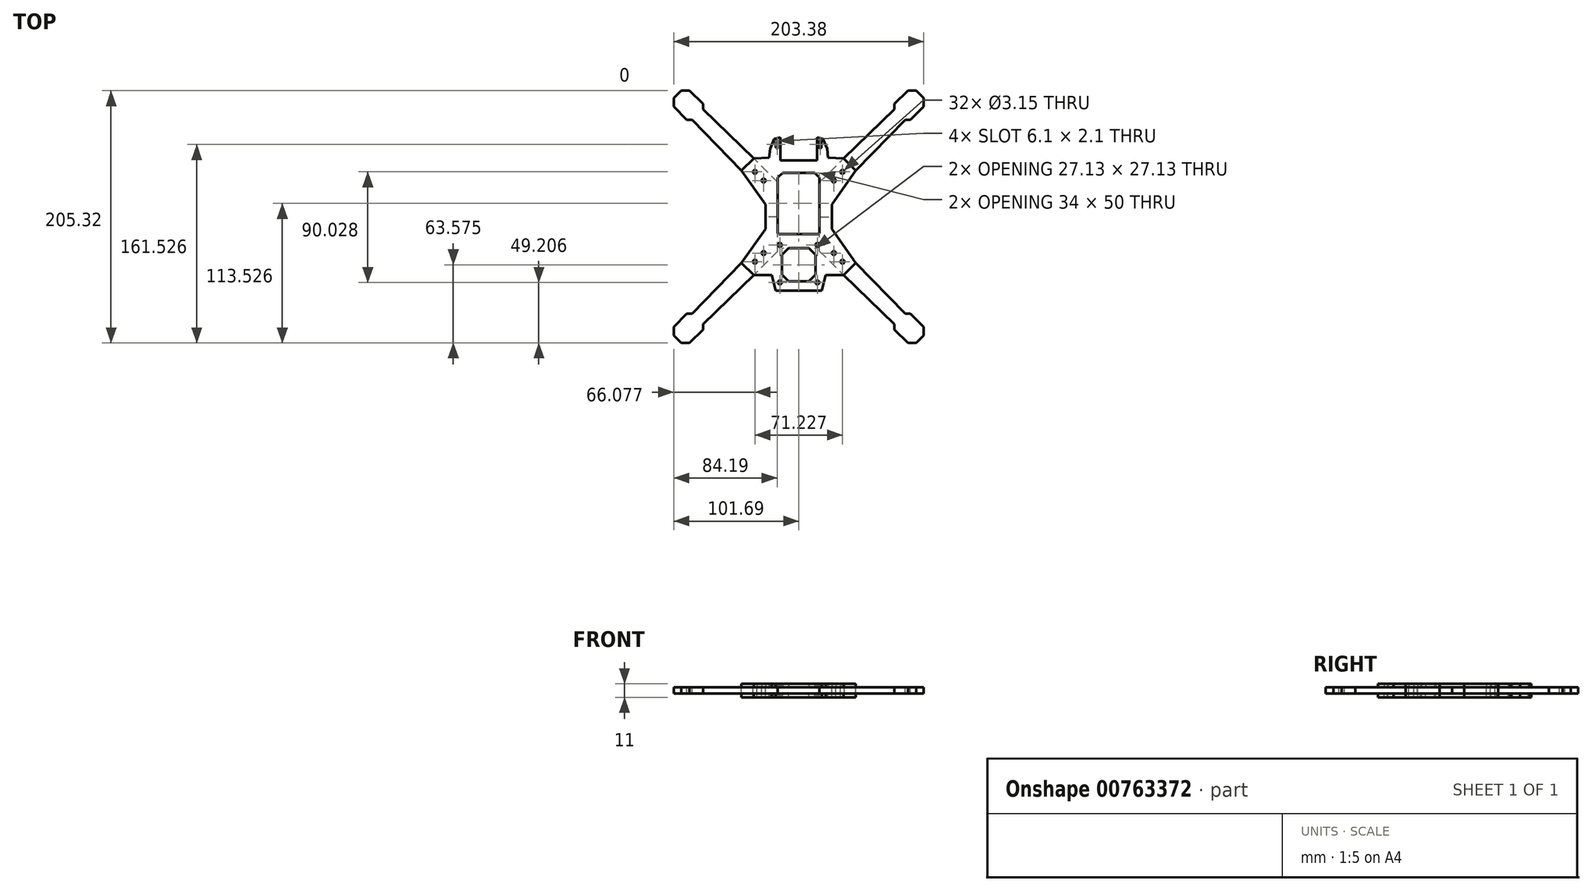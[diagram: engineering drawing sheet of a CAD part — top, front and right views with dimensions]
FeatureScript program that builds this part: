
annotation { "Feature Type Name" : "Feature", "Feature Type Description" : "" }
export const myFeature = defineFeature(function(context is Context, id is Id, definition is map)
    precondition{}
    {
        {
            assignVariable(context, id + "F0", {"name" : "SandwichThickness", "anyValue" : 3 * mm});
        }
        {
            assignVariable(context, id + "F1", {"name" : "ArmThickness", "anyValue" : 5 * mm});
        }
        {
            var Q0;
            Q0=qCreatedBy(makeId("Top.planeOp"),FACE);
            var sketch = newSketch(context, id + "F2", { "sketchPlane" : qUnion([Q0])});
            skCircle(sketch, "E0", {"center": v(-15.25, -22.95) * mm, "radius": 1.57 * mm});
            skCircle(sketch, "E1.MirrorC", {"center": v(15.25, -22.95) * mm, "radius": 1.57 * mm});
            skCircle(sketch, "E2", {"center": v(-15.25, -53.45) * mm, "radius": 1.57 * mm});
            skCircle(sketch, "E3.MirrorC", {"center": v(15.25, -53.45) * mm, "radius": 1.57 * mm});
            skLineSegment(sketch, "E4", {"start": v(-19.86, 63.27) * mm, "end": v(-23.2, 55.32) * mm});
            skLineSegment(sketch, "E5", {"start": v(-19.86, 63.27) * mm, "end": v(-15, 64.52) * mm});
            skLineSegment(sketch, "E6", {"start": v(-15, 64.52) * mm, "end": v(-15, 45.87) * mm});
            skLineSegment(sketch, "E7", {"start": v(-17, 31.8) * mm, "end": v(-17, -13.31) * mm});
            skLineSegment(sketch, "E8", {"start": v(-17, -13.31) * mm, "end": v(-16.18, -14.13) * mm});
            skLineSegment(sketch, "E9", {"start": v(-16.18, -14.13) * mm, "end": v(0, -14.13) * mm});
            skLineSegment(sketch, "E10.MirrorCS", {"start": v(14.55, -15.76) * mm, "end": v(0, -15.76) * mm});
            skArc(sketch, "E11.0.startCap", {"start": v(-18.55, 60.87) * mm, "mid": v(-17.5, 61.92) * mm, "end": v(-16.45, 60.87) * mm});
            skArc(sketch, "E11.0.endCap", {"start": v(-16.45, 56.87) * mm, "mid": v(-17.5, 55.82) * mm, "end": v(-18.55, 56.87) * mm});
            skLineSegment(sketch, "E11.0.left", {"start": v(-16.45, 60.87) * mm, "end": v(-16.45, 56.87) * mm});
            skLineSegment(sketch, "E11.0.right", {"start": v(-18.55, 60.87) * mm, "end": v(-18.55, 56.87) * mm});
            skLineSegment(sketch, "E12", {"start": v(0, 35.87) * mm, "end": v(-12.93, 35.87) * mm});
            skLineSegment(sketch, "E13", {"start": v(-12.93, 35.87) * mm, "end": v(-17, 31.8) * mm});
            skLineSegment(sketch, "E14", {"start": v(-36.6, 47.46) * mm, "end": v(-46.5, 37.56) * mm});
            skLineSegment(sketch, "E15", {"start": v(-46.5, 37.56) * mm, "end": v(-27, 10) * mm});
            skLineSegment(sketch, "E16", {"start": v(-27, 10) * mm, "end": v(-27, -10) * mm});
            skLineSegment(sketch, "E17", {"start": v(-27, -10) * mm, "end": v(-46.5, -37.56) * mm});
            skLineSegment(sketch, "E18", {"start": v(-46.5, -37.56) * mm, "end": v(-36.6, -47.46) * mm});
            skLineSegment(sketch, "E19", {"start": v(-36.6, -47.46) * mm, "end": v(-21.87, -47.46) * mm});
            skLineSegment(sketch, "E20", {"start": v(-21.87, -47.46) * mm, "end": v(-18.77, -60.18) * mm});
            skLineSegment(sketch, "E21", {"start": v(-18.77, -60.18) * mm, "end": v(0, -60.18) * mm});
            skLineSegment(sketch, "E22", {"start": v(-36.6, 47.46) * mm, "end": v(-23.99, 48.25) * mm});
            skLineSegment(sketch, "E23", {"start": v(-23.99, 48.25) * mm, "end": v(-23.2, 55.32) * mm});
            skCircle(sketch, "E24", {"center": v(-35.61, 36.57) * mm, "radius": 1.57 * mm});
            skLineSegment(sketch, "E25", {"start": v(-41.55, 42.51) * mm, "end": v(-28.54, 29.5) * mm, "construction": true});
            skCircle(sketch, "E26", {"center": v(-28.54, 29.5) * mm, "radius": 1.57 * mm});
            skLineSegment(sketch, "E27", {"start": v(-41.55, -42.51) * mm, "end": v(-28.54, -29.5) * mm, "construction": true});
            skLineSegment(sketch, "E28", {"start": v(-28.54, 29.5) * mm, "end": v(-28.54, -29.5) * mm, "construction": true});
            skLineSegment(sketch, "E29", {"start": v(-68.87, 0) * mm, "end": v(73.63, 0) * mm, "construction": true});
            skPoint(sketch, "E29.startSnap0", {"position": v(-28.54, 0) * mm});
            skCircle(sketch, "E30.MirrorC", {"center": v(-28.54, -29.5) * mm, "radius": 1.57 * mm});
            skCircle(sketch, "E31.MirrorC", {"center": v(-35.61, -36.57) * mm, "radius": 1.57 * mm});
            skLineSegment(sketch, "E32", {"start": v(18.01, -39.09) * mm, "end": v(-13.57, -39.09) * mm, "construction": true});
            skLineSegment(sketch, "E33", {"start": v(-13.57, -39.09) * mm, "end": v(-13.57, -47.25) * mm});
            skLineSegment(sketch, "E34", {"start": v(-13.57, -47.25) * mm, "end": v(-8.16, -52.65) * mm});
            skLineSegment(sketch, "E35", {"start": v(-8.16, -52.65) * mm, "end": v(0, -52.65) * mm});
            skLineSegment(sketch, "E36.MirrorCS", {"start": v(13.57, -39.09) * mm, "end": v(13.57, -47.25) * mm});
            skLineSegment(sketch, "E37.MirrorCS", {"start": v(13.57, -47.25) * mm, "end": v(8.16, -52.65) * mm});
            skLineSegment(sketch, "E38.MirrorCS", {"start": v(8.16, -52.65) * mm, "end": v(0, -52.65) * mm});
            skLineSegment(sketch, "E39.MirrorCS", {"start": v(-13.57, -39.09) * mm, "end": v(-13.57, -30.92) * mm});
            skLineSegment(sketch, "E40.MirrorCS", {"start": v(-13.57, -30.92) * mm, "end": v(-8.16, -25.52) * mm});
            skLineSegment(sketch, "E41.MirrorCS", {"start": v(-8.16, -25.52) * mm, "end": v(0, -25.52) * mm});
            skLineSegment(sketch, "E42.MirrorCS", {"start": v(8.16, -25.52) * mm, "end": v(0, -25.52) * mm});
            skLineSegment(sketch, "E43.MirrorCS", {"start": v(13.57, -30.92) * mm, "end": v(8.16, -25.52) * mm});
            skLineSegment(sketch, "E44.MirrorCS", {"start": v(13.57, -39.09) * mm, "end": v(13.57, -30.92) * mm});
            skLineSegment(sketch, "E45.MirrorCS", {"start": v(15, 64.52) * mm, "end": v(15, 45.87) * mm});
            skLineSegment(sketch, "E46.MirrorCS", {"start": v(19.86, 63.27) * mm, "end": v(15, 64.52) * mm});
            skLineSegment(sketch, "E47.MirrorCS", {"start": v(19.86, 63.27) * mm, "end": v(23.2, 55.32) * mm});
            skArc(sketch, "E48.MirrorCS", {"start": v(18.55, 60.87) * mm, "mid": v(17.5, 61.92) * mm, "end": v(16.45, 60.87) * mm});
            skLineSegment(sketch, "E49.MirrorCS", {"start": v(17.5, 60.87) * mm, "end": v(17.5, 56.87) * mm, "construction": true});
            skLineSegment(sketch, "E50.MirrorCS", {"start": v(18.55, 60.87) * mm, "end": v(18.55, 56.87) * mm});
            skLineSegment(sketch, "E51.MirrorCS", {"start": v(16.45, 60.87) * mm, "end": v(16.45, 56.87) * mm});
            skArc(sketch, "E52.MirrorCS", {"start": v(16.45, 56.87) * mm, "mid": v(17.5, 55.82) * mm, "end": v(18.55, 56.87) * mm});
            skLineSegment(sketch, "E53.MirrorCS", {"start": v(23.99, 48.25) * mm, "end": v(23.2, 55.32) * mm});
            skLineSegment(sketch, "E54.MirrorCS", {"start": v(36.6, 47.46) * mm, "end": v(23.99, 48.25) * mm});
            skLineSegment(sketch, "E55.MirrorCS", {"start": v(36.6, 47.46) * mm, "end": v(46.5, 37.56) * mm});
            skLineSegment(sketch, "E56.MirrorCS", {"start": v(46.5, 37.56) * mm, "end": v(27, 10) * mm});
            skCircle(sketch, "E57.MirrorC", {"center": v(35.61, 36.57) * mm, "radius": 1.57 * mm});
            skCircle(sketch, "E58.MirrorC", {"center": v(28.54, 29.5) * mm, "radius": 1.57 * mm});
            skCircle(sketch, "E59.MirrorC", {"center": v(28.54, -29.5) * mm, "radius": 1.57 * mm});
            skCircle(sketch, "E60.MirrorC", {"center": v(35.61, -36.57) * mm, "radius": 1.57 * mm});
            skLineSegment(sketch, "E61.MirrorCS", {"start": v(27, -10) * mm, "end": v(46.5, -37.56) * mm});
            skLineSegment(sketch, "E62.MirrorCS", {"start": v(27, 10) * mm, "end": v(27, -10) * mm});
            skLineSegment(sketch, "E63.MirrorCS", {"start": v(46.5, -37.56) * mm, "end": v(36.6, -47.46) * mm});
            skLineSegment(sketch, "E64.MirrorCS", {"start": v(36.6, -47.46) * mm, "end": v(21.87, -47.46) * mm});
            skLineSegment(sketch, "E65.MirrorCS", {"start": v(21.87, -47.46) * mm, "end": v(18.77, -60.18) * mm});
            skLineSegment(sketch, "E66.MirrorCS", {"start": v(18.77, -60.18) * mm, "end": v(0, -60.18) * mm});
            skPoint(sketch, "E67", {"position": v(-17.5, 58.87) * mm});
            skLineSegment(sketch, "E68.MirrorCS", {"start": v(0, 35.87) * mm, "end": v(12.93, 35.87) * mm});
            skLineSegment(sketch, "E69.MirrorCS", {"start": v(12.93, 35.87) * mm, "end": v(17, 31.8) * mm});
            skLineSegment(sketch, "E70.MirrorCS", {"start": v(17, 31.8) * mm, "end": v(17, -13.31) * mm});
            skLineSegment(sketch, "E71.MirrorCS", {"start": v(16.18, -14.13) * mm, "end": v(0, -14.13) * mm});
            skLineSegment(sketch, "E72.MirrorCS", {"start": v(17, -13.31) * mm, "end": v(16.18, -14.13) * mm});
            skLineSegment(sketch, "E73", {"start": v(-17.5, 60.87) * mm, "end": v(-17.5, 56.87) * mm, "construction": true});
            skLineSegment(sketch, "E74", {"start": v(-15, 45.87) * mm, "end": v(0, 45.87) * mm});
            skLineSegment(sketch, "E75.MirrorCS", {"start": v(15, 45.87) * mm, "end": v(0, 45.87) * mm});
            skSolve(sketch);
        }
        {
            var Q0;
            Q0=makeQuery(id+"F2.imprint","IMPRINT",FACE,{"disambiguationData":[TD([[makeQuery(id+"F2.imprint","IMPRINT",EDGE,{"derivedFrom":sQuery(id+"F2.wireOp",EDGE,"E0")}),-1.0]])]});
            var sketch = newSketch(context, id + "F3", { "sketchPlane" : qUnion([Q0])});
            skCircle(sketch, "E76.0", {"center": v(-35.61, 36.57) * mm, "radius": 1.57 * mm});
            skCircle(sketch, "E77.0", {"center": v(-28.54, 29.5) * mm, "radius": 1.57 * mm});
            skLineSegment(sketch, "E78.0", {"start": v(-46.5, 37.56) * mm, "end": v(-27, 10) * mm});
            skPoint(sketch, "E79.0", {"position": v(-36.6, 47.46) * mm});
            skLineSegment(sketch, "E80", {"start": v(-17, 28.03) * mm, "end": v(-36.6, 47.46) * mm});
            skLineSegment(sketch, "E81", {"start": v(-36.6, 47.46) * mm, "end": v(-77.83, 87.54) * mm});
            skLineSegment(sketch, "E82.MirrorCS", {"start": v(-46.5, 37.56) * mm, "end": v(-86.58, 78.8) * mm});
            skLineSegment(sketch, "E83", {"start": v(-77.83, 87.54) * mm, "end": v(-77.83, 91.94) * mm});
            skLineSegment(sketch, "E84", {"start": v(-77.83, 91.94) * mm, "end": v(-88.86, 102.66) * mm});
            skLineSegment(sketch, "E85", {"start": v(-88.86, 102.66) * mm, "end": v(-95.6, 102.66) * mm});
            skLineSegment(sketch, "E86.MirrorCS", {"start": v(-86.58, 78.8) * mm, "end": v(-90.98, 78.8) * mm});
            skLineSegment(sketch, "E87.MirrorCS", {"start": v(-90.98, 78.8) * mm, "end": v(-101.7, 89.82) * mm});
            skLineSegment(sketch, "E88.MirrorCS", {"start": v(-101.7, 89.82) * mm, "end": v(-101.7, 96.57) * mm});
            skLineSegment(sketch, "E89", {"start": v(-95.6, 102.66) * mm, "end": v(-101.7, 96.57) * mm});
            skLineSegment(sketch, "E90", {"start": v(-27, 10) * mm, "end": v(-27, 0) * mm});
            skLineSegment(sketch, "E91", {"start": v(-17, 0) * mm, "end": v(-27, 0) * mm});
            skLineSegment(sketch, "E92", {"start": v(-17, 28.03) * mm, "end": v(-17, 0) * mm});
            skSolve(sketch);
        }
        {
            var Q0;
            Q0 = qSketchRegion(id + "F2", true);
            extrude(context, id + "F4", {"entities" : qUnion([Q0]), "depth" : getVariable(context, 'SandwichThickness'), "offsetDistance" : 25 * mm});
        }
        {
            var Q0;
            Q0 = qSketchRegion(id + "F3", true);
            extrude(context, id + "F5", {"entities" : qUnion([Q0]), "oppositeDirection" : true, "depth" : getVariable(context, 'ArmThickness'), "offsetDistance" : 25 * mm});
        }
        {
            var Q0;
            Q0=makeQuery(id+"F5.opExtrude","SWEPT_BODY",BODY,{"disambiguationData":[OSD([sQuery(id+"F3.wireOp",EDGE,"E76.0"),sQuery(id+"F3.wireOp",EDGE,"E77.0"),sQuery(id+"F3.wireOp",EDGE,"E78.0"),sQuery(id+"F3.wireOp",EDGE,"ryfLNu9Q-lvBm-nTtp-5XZK-GBmvkfGpwlt8"),sQuery(id+"F3.wireOp",EDGE,"jJSJpg1Z-H1VB-TZbG-EUJu-PynuGd8tt2l3"),sQuery(id+"F3.wireOp",EDGE,"NvUQPJ1X-drPx-f47S-Xc06-5eFbwI9bCRaz"),sQuery(id+"F3.wireOp",EDGE,"E80"),sQuery(id+"F3.wireOp",EDGE,"E81"),sQuery(id+"F3.wireOp",EDGE,"E82.MirrorCS"),sQuery(id+"F3.wireOp",EDGE,"E83"),sQuery(id+"F3.wireOp",EDGE,"E84"),sQuery(id+"F3.wireOp",EDGE,"E85"),sQuery(id+"F3.wireOp",EDGE,"E86.MirrorCS"),sQuery(id+"F3.wireOp",EDGE,"E87.MirrorCS"),sQuery(id+"F3.wireOp",EDGE,"E88.MirrorCS"),sQuery(id+"F3.wireOp",EDGE,"E89")])]});
            var Q1;
            Q1=qCreatedBy(makeId("Right.planeOp"),FACE);
            mirror(context, id + "F6", {"entities" : qUnion([Q0]), "mirrorPlane" : qUnion([Q1])});
        }
        {
            var Q0;
            Q0=makeQuery(id+"F5.opExtrude","SWEPT_BODY",BODY,{"disambiguationData":[OSD([sQuery(id+"F3.wireOp",EDGE,"E76.0"),sQuery(id+"F3.wireOp",EDGE,"E77.0"),sQuery(id+"F3.wireOp",EDGE,"E78.0"),sQuery(id+"F3.wireOp",EDGE,"ryfLNu9Q-lvBm-nTtp-5XZK-GBmvkfGpwlt8"),sQuery(id+"F3.wireOp",EDGE,"jJSJpg1Z-H1VB-TZbG-EUJu-PynuGd8tt2l3"),sQuery(id+"F3.wireOp",EDGE,"NvUQPJ1X-drPx-f47S-Xc06-5eFbwI9bCRaz"),sQuery(id+"F3.wireOp",EDGE,"E80"),sQuery(id+"F3.wireOp",EDGE,"E81"),sQuery(id+"F3.wireOp",EDGE,"E82.MirrorCS"),sQuery(id+"F3.wireOp",EDGE,"E83"),sQuery(id+"F3.wireOp",EDGE,"E84"),sQuery(id+"F3.wireOp",EDGE,"E85"),sQuery(id+"F3.wireOp",EDGE,"E86.MirrorCS"),sQuery(id+"F3.wireOp",EDGE,"E87.MirrorCS"),sQuery(id+"F3.wireOp",EDGE,"E88.MirrorCS"),sQuery(id+"F3.wireOp",EDGE,"E89")])]});
            var Q1;
            Q1=makeQuery(id+"F6.opPattern","COPY",BODY,{"derivedFrom":makeQuery(id+"F5.opExtrude","SWEPT_BODY",BODY,{"disambiguationData":[OSD([sQuery(id+"F3.wireOp",EDGE,"E76.0"),sQuery(id+"F3.wireOp",EDGE,"E77.0"),sQuery(id+"F3.wireOp",EDGE,"E78.0"),sQuery(id+"F3.wireOp",EDGE,"ryfLNu9Q-lvBm-nTtp-5XZK-GBmvkfGpwlt8"),sQuery(id+"F3.wireOp",EDGE,"jJSJpg1Z-H1VB-TZbG-EUJu-PynuGd8tt2l3"),sQuery(id+"F3.wireOp",EDGE,"NvUQPJ1X-drPx-f47S-Xc06-5eFbwI9bCRaz"),sQuery(id+"F3.wireOp",EDGE,"E80"),sQuery(id+"F3.wireOp",EDGE,"E81"),sQuery(id+"F3.wireOp",EDGE,"E82.MirrorCS"),sQuery(id+"F3.wireOp",EDGE,"E83"),sQuery(id+"F3.wireOp",EDGE,"E84"),sQuery(id+"F3.wireOp",EDGE,"E85"),sQuery(id+"F3.wireOp",EDGE,"E86.MirrorCS"),sQuery(id+"F3.wireOp",EDGE,"E87.MirrorCS"),sQuery(id+"F3.wireOp",EDGE,"E88.MirrorCS"),sQuery(id+"F3.wireOp",EDGE,"E89")])]}),"instanceName":"1"});
            var Q2;
            Q2=qCreatedBy(makeId("Front.planeOp"),FACE);
            mirror(context, id + "F7", {"entities" : qUnion([Q0, Q1]), "mirrorPlane" : qUnion([Q2])});
        }
        {
            var Q0;
            Q0=makeQuery(id+"F4.opExtrude","CAP_FACE",FACE,{"disambiguationData":[OSD([sQuery(id+"F2.wireOp",EDGE,"E0"),sQuery(id+"F2.wireOp",EDGE,"E1.MirrorC"),sQuery(id+"F2.wireOp",EDGE,"E2"),sQuery(id+"F2.wireOp",EDGE,"E3.MirrorC"),sQuery(id+"F2.wireOp",EDGE,"E4"),sQuery(id+"F2.wireOp",EDGE,"E5"),sQuery(id+"F2.wireOp",EDGE,"E6"),sQuery(id+"F2.wireOp",EDGE,"E7"),sQuery(id+"F2.wireOp",EDGE,"E8"),sQuery(id+"F2.wireOp",EDGE,"E9"),sQuery(id+"F2.wireOp",EDGE,"e5299873-a759-4b57-8e80-d9d10e7549ee3.MirrorCS"),sQuery(id+"F2.wireOp",EDGE,"E10.MirrorCS"),sQuery(id+"F2.wireOp",EDGE,"e5299873-a759-4b57-8e80-d9d10e7549ee9.MirrorCS"),sQuery(id+"F2.wireOp",EDGE,"E11.0.startCap"),sQuery(id+"F2.wireOp",EDGE,"E11.0.endCap"),sQuery(id+"F2.wireOp",EDGE,"E11.0.left"),sQuery(id+"F2.wireOp",EDGE,"E11.0.right"),sQuery(id+"F2.wireOp",EDGE,"E12"),sQuery(id+"F2.wireOp",EDGE,"E13"),sQuery(id+"F2.wireOp",EDGE,"9a270ce7-c52f-46a5-af98-66fd616d05850.MirrorCS"),sQuery(id+"F2.wireOp",EDGE,"67116adb-6c2d-4a79-b561-e3b161ec186f0.MirrorCS"),sQuery(id+"F2.wireOp",EDGE,"E14"),sQuery(id+"F2.wireOp",EDGE,"E15"),sQuery(id+"F2.wireOp",EDGE,"E16"),sQuery(id+"F2.wireOp",EDGE,"E17"),sQuery(id+"F2.wireOp",EDGE,"E18"),sQuery(id+"F2.wireOp",EDGE,"E19"),sQuery(id+"F2.wireOp",EDGE,"E20"),sQuery(id+"F2.wireOp",EDGE,"E21"),sQuery(id+"F2.wireOp",EDGE,"1nEM5pcN-P6g0-HtUo-ixTz-kLAk9SliolJh"),sQuery(id+"F2.wireOp",EDGE,"uqU8zYV3-j0Yk-oc9d-4yJz-UkPliC03LPk7"),sQuery(id+"F2.wireOp",EDGE,"E22"),sQuery(id+"F2.wireOp",EDGE,"E23"),sQuery(id+"F2.wireOp",EDGE,"E24"),sQuery(id+"F2.wireOp",EDGE,"E26"),sQuery(id+"F2.wireOp",EDGE,"E30.MirrorC"),sQuery(id+"F2.wireOp",EDGE,"E31.MirrorC"),sQuery(id+"F2.wireOp",EDGE,"E33"),sQuery(id+"F2.wireOp",EDGE,"E34"),sQuery(id+"F2.wireOp",EDGE,"E35"),sQuery(id+"F2.wireOp",EDGE,"E36.MirrorCS"),sQuery(id+"F2.wireOp",EDGE,"E37.MirrorCS"),sQuery(id+"F2.wireOp",EDGE,"E38.MirrorCS"),sQuery(id+"F2.wireOp",EDGE,"E39.MirrorCS"),sQuery(id+"F2.wireOp",EDGE,"E40.MirrorCS"),sQuery(id+"F2.wireOp",EDGE,"E41.MirrorCS"),sQuery(id+"F2.wireOp",EDGE,"E42.MirrorCS"),sQuery(id+"F2.wireOp",EDGE,"E43.MirrorCS"),sQuery(id+"F2.wireOp",EDGE,"E44.MirrorCS"),sQuery(id+"F2.wireOp",EDGE,"93611096-e643-452b-bf63-19d234b5ac6d0.MirrorCS"),sQuery(id+"F2.wireOp",EDGE,"9a390328-94e8-4b27-83f3-3fab0f602b6f0.MirrorCS"),sQuery(id+"F2.wireOp",EDGE,"E45.MirrorCS"),sQuery(id+"F2.wireOp",EDGE,"E46.MirrorCS"),sQuery(id+"F2.wireOp",EDGE,"E47.MirrorCS"),sQuery(id+"F2.wireOp",EDGE,"E48.MirrorCS"),sQuery(id+"F2.wireOp",EDGE,"E50.MirrorCS"),sQuery(id+"F2.wireOp",EDGE,"E51.MirrorCS"),sQuery(id+"F2.wireOp",EDGE,"E52.MirrorCS"),sQuery(id+"F2.wireOp",EDGE,"E53.MirrorCS"),sQuery(id+"F2.wireOp",EDGE,"E54.MirrorCS"),sQuery(id+"F2.wireOp",EDGE,"E55.MirrorCS"),sQuery(id+"F2.wireOp",EDGE,"E56.MirrorCS"),sQuery(id+"F2.wireOp",EDGE,"E57.MirrorC"),sQuery(id+"F2.wireOp",EDGE,"E58.MirrorC"),sQuery(id+"F2.wireOp",EDGE,"E59.MirrorC"),sQuery(id+"F2.wireOp",EDGE,"E60.MirrorC"),sQuery(id+"F2.wireOp",EDGE,"E61.MirrorCS"),sQuery(id+"F2.wireOp",EDGE,"E62.MirrorCS"),sQuery(id+"F2.wireOp",EDGE,"E63.MirrorCS"),sQuery(id+"F2.wireOp",EDGE,"E64.MirrorCS"),sQuery(id+"F2.wireOp",EDGE,"E65.MirrorCS"),sQuery(id+"F2.wireOp",EDGE,"E66.MirrorCS")])],"isStart":true});
            cPlane(context, id + "F8", {"entities" : qUnion([Q0]), "cplaneType" : CPlaneType.OFFSET, "offset" : getVariable(context, 'ArmThickness') / 2, "width" : 150 * mm, "height" : 150 * mm});
        }
        {
            var Q0;
            Q0=makeQuery(id+"F4.opExtrude","SWEPT_BODY",BODY,{"disambiguationData":[OSD([sQuery(id+"F2.wireOp",EDGE,"E0"),sQuery(id+"F2.wireOp",EDGE,"E1.MirrorC"),sQuery(id+"F2.wireOp",EDGE,"E2"),sQuery(id+"F2.wireOp",EDGE,"E3.MirrorC"),sQuery(id+"F2.wireOp",EDGE,"E4"),sQuery(id+"F2.wireOp",EDGE,"E5"),sQuery(id+"F2.wireOp",EDGE,"E6"),sQuery(id+"F2.wireOp",EDGE,"E7"),sQuery(id+"F2.wireOp",EDGE,"E8"),sQuery(id+"F2.wireOp",EDGE,"E9"),sQuery(id+"F2.wireOp",EDGE,"e5299873-a759-4b57-8e80-d9d10e7549ee3.MirrorCS"),sQuery(id+"F2.wireOp",EDGE,"E10.MirrorCS"),sQuery(id+"F2.wireOp",EDGE,"e5299873-a759-4b57-8e80-d9d10e7549ee9.MirrorCS"),sQuery(id+"F2.wireOp",EDGE,"E11.0.startCap"),sQuery(id+"F2.wireOp",EDGE,"E11.0.endCap"),sQuery(id+"F2.wireOp",EDGE,"E11.0.left"),sQuery(id+"F2.wireOp",EDGE,"E11.0.right"),sQuery(id+"F2.wireOp",EDGE,"E12"),sQuery(id+"F2.wireOp",EDGE,"E13"),sQuery(id+"F2.wireOp",EDGE,"9a270ce7-c52f-46a5-af98-66fd616d05850.MirrorCS"),sQuery(id+"F2.wireOp",EDGE,"67116adb-6c2d-4a79-b561-e3b161ec186f0.MirrorCS"),sQuery(id+"F2.wireOp",EDGE,"E14"),sQuery(id+"F2.wireOp",EDGE,"E15"),sQuery(id+"F2.wireOp",EDGE,"E16"),sQuery(id+"F2.wireOp",EDGE,"E17"),sQuery(id+"F2.wireOp",EDGE,"E18"),sQuery(id+"F2.wireOp",EDGE,"E19"),sQuery(id+"F2.wireOp",EDGE,"E20"),sQuery(id+"F2.wireOp",EDGE,"E21"),sQuery(id+"F2.wireOp",EDGE,"1nEM5pcN-P6g0-HtUo-ixTz-kLAk9SliolJh"),sQuery(id+"F2.wireOp",EDGE,"uqU8zYV3-j0Yk-oc9d-4yJz-UkPliC03LPk7"),sQuery(id+"F2.wireOp",EDGE,"E22"),sQuery(id+"F2.wireOp",EDGE,"E23"),sQuery(id+"F2.wireOp",EDGE,"E24"),sQuery(id+"F2.wireOp",EDGE,"E26"),sQuery(id+"F2.wireOp",EDGE,"E30.MirrorC"),sQuery(id+"F2.wireOp",EDGE,"E31.MirrorC"),sQuery(id+"F2.wireOp",EDGE,"E33"),sQuery(id+"F2.wireOp",EDGE,"E34"),sQuery(id+"F2.wireOp",EDGE,"E35"),sQuery(id+"F2.wireOp",EDGE,"E36.MirrorCS"),sQuery(id+"F2.wireOp",EDGE,"E37.MirrorCS"),sQuery(id+"F2.wireOp",EDGE,"E38.MirrorCS"),sQuery(id+"F2.wireOp",EDGE,"E39.MirrorCS"),sQuery(id+"F2.wireOp",EDGE,"E40.MirrorCS"),sQuery(id+"F2.wireOp",EDGE,"E41.MirrorCS"),sQuery(id+"F2.wireOp",EDGE,"E42.MirrorCS"),sQuery(id+"F2.wireOp",EDGE,"E43.MirrorCS"),sQuery(id+"F2.wireOp",EDGE,"E44.MirrorCS"),sQuery(id+"F2.wireOp",EDGE,"93611096-e643-452b-bf63-19d234b5ac6d0.MirrorCS"),sQuery(id+"F2.wireOp",EDGE,"9a390328-94e8-4b27-83f3-3fab0f602b6f0.MirrorCS"),sQuery(id+"F2.wireOp",EDGE,"E45.MirrorCS"),sQuery(id+"F2.wireOp",EDGE,"E46.MirrorCS"),sQuery(id+"F2.wireOp",EDGE,"E47.MirrorCS"),sQuery(id+"F2.wireOp",EDGE,"E48.MirrorCS"),sQuery(id+"F2.wireOp",EDGE,"E50.MirrorCS"),sQuery(id+"F2.wireOp",EDGE,"E51.MirrorCS"),sQuery(id+"F2.wireOp",EDGE,"E52.MirrorCS"),sQuery(id+"F2.wireOp",EDGE,"E53.MirrorCS"),sQuery(id+"F2.wireOp",EDGE,"E54.MirrorCS"),sQuery(id+"F2.wireOp",EDGE,"E55.MirrorCS"),sQuery(id+"F2.wireOp",EDGE,"E56.MirrorCS"),sQuery(id+"F2.wireOp",EDGE,"E57.MirrorC"),sQuery(id+"F2.wireOp",EDGE,"E58.MirrorC"),sQuery(id+"F2.wireOp",EDGE,"E59.MirrorC"),sQuery(id+"F2.wireOp",EDGE,"E60.MirrorC"),sQuery(id+"F2.wireOp",EDGE,"E61.MirrorCS"),sQuery(id+"F2.wireOp",EDGE,"E62.MirrorCS"),sQuery(id+"F2.wireOp",EDGE,"E63.MirrorCS"),sQuery(id+"F2.wireOp",EDGE,"E64.MirrorCS"),sQuery(id+"F2.wireOp",EDGE,"E65.MirrorCS"),sQuery(id+"F2.wireOp",EDGE,"E66.MirrorCS")])]});
            var Q1;
            Q1=qCreatedBy(id+"F8.planeOp",FACE);
            mirror(context, id + "F9", {"entities" : qUnion([Q0]), "mirrorPlane" : qUnion([Q1])});
        }
    });
